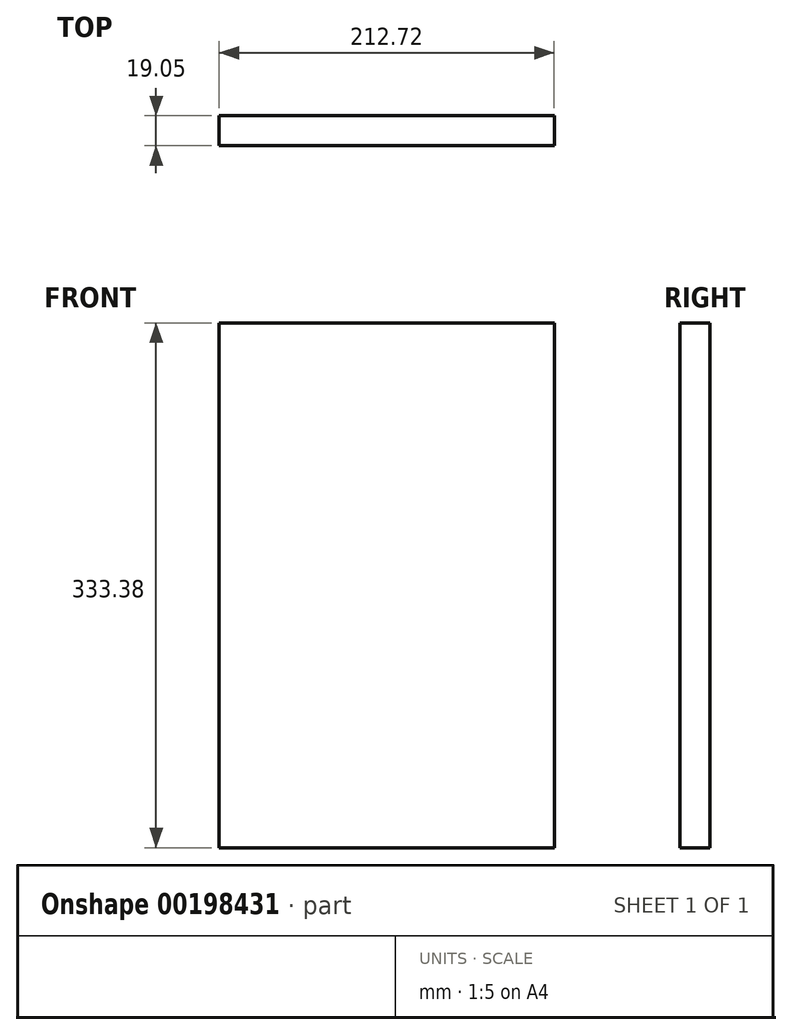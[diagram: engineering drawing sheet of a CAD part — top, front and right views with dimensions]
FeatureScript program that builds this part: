
annotation { "Feature Type Name" : "Feature", "Feature Type Description" : "" }
export const myFeature = defineFeature(function(context is Context, id is Id, definition is map)
    precondition{}
    {
        {
            var Q0;
            Q0=qCreatedBy(makeId("Front.planeOp"),FACE);
            var sketch = newSketch(context, id + "F0", { "sketchPlane" : qUnion([Q0])});
            skLineSegment(sketch, "E0.bottom", {"start": v(0, 0) * mm, "end": v(212.72, 0) * mm});
            skLineSegment(sketch, "E0.top", {"start": v(0, 333.38) * mm, "end": v(212.72, 333.38) * mm});
            skLineSegment(sketch, "E0.left", {"start": v(0, 0) * mm, "end": v(0, 333.38) * mm});
            skLineSegment(sketch, "E0.right", {"start": v(212.72, 0) * mm, "end": v(212.72, 333.38) * mm});
            skSolve(sketch);
        }
        {
            var Q0;
            Q0=makeQuery(id+"F0.imprint","IMPRINT",FACE,{"disambiguationData":[TD([[makeQuery(id+"F0.imprint","IMPRINT",EDGE,{"derivedFrom":sQuery(id+"F0.wireOp",EDGE,"E0.bottom")}),1.0]])]});
            extrude(context, id + "F1", {"entities" : qUnion([Q0]), "depth" : 19.05 * mm});
        }
    });
